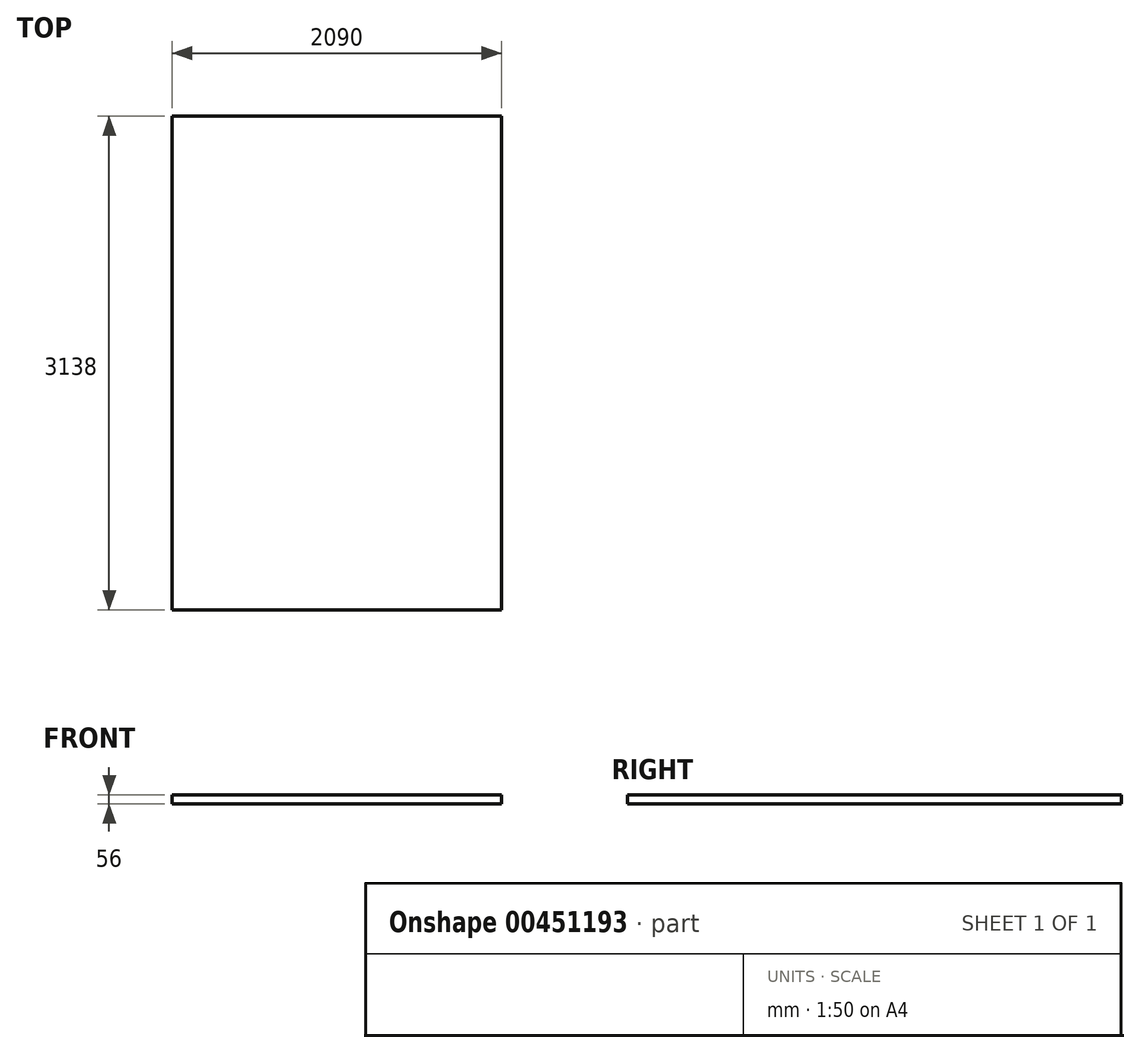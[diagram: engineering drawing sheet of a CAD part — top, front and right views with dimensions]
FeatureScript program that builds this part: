
annotation { "Feature Type Name" : "Feature", "Feature Type Description" : "" }
export const myFeature = defineFeature(function(context is Context, id is Id, definition is map)
    precondition{}
    {
        {
            var Q0;
            Q0=qCreatedBy(makeId("Top.planeOp"),FACE);
            var sketch = newSketch(context, id + "F0", { "sketchPlane" : qUnion([Q0])});
            skLineSegment(sketch, "E0.bottom", {"start": v(1045, -1569) * mm, "end": v(-1045, -1569) * mm});
            skLineSegment(sketch, "E0.top", {"start": v(1045, 1569) * mm, "end": v(-1045, 1569) * mm});
            skLineSegment(sketch, "E0.left", {"start": v(1045, -1569) * mm, "end": v(1045, 1569) * mm});
            skLineSegment(sketch, "E0.right", {"start": v(-1045, -1569) * mm, "end": v(-1045, 1569) * mm});
            skPoint(sketch, "E0.middle", {"position": v(0, 0) * mm});
            skSolve(sketch);
        }
        {
            var Q0;
            Q0 = qSketchRegion(id + "F0", true);
            extrude(context, id + "F1", {"entities" : qUnion([Q0]), "depth" : 56 * mm, "offsetDistance" : 25 * mm});
        }
    });
